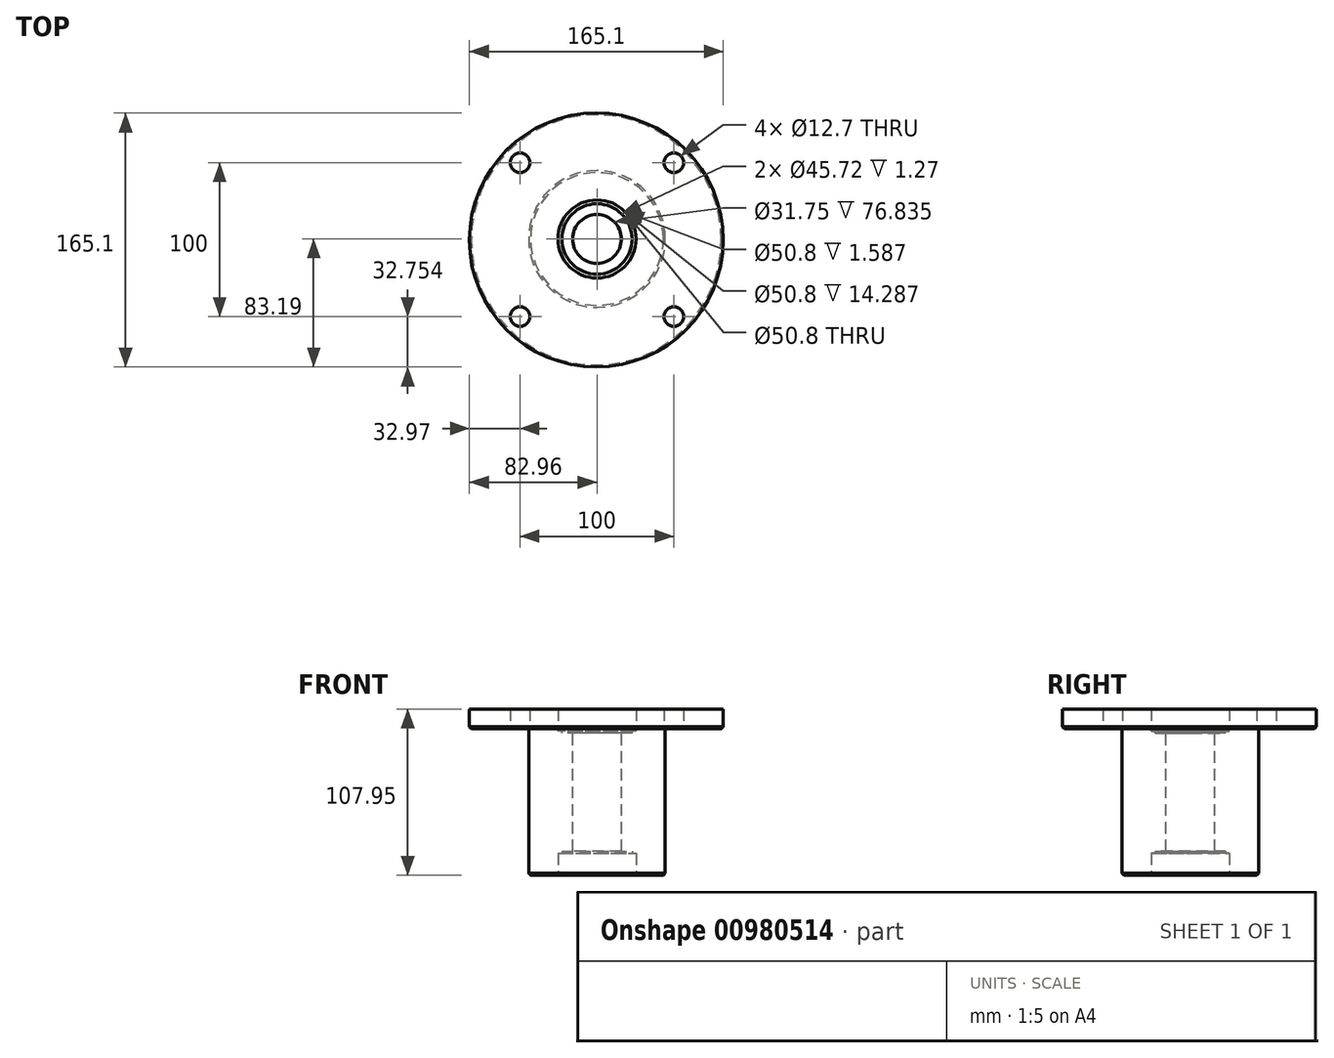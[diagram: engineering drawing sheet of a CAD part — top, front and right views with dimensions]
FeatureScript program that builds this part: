
annotation { "Feature Type Name" : "Feature", "Feature Type Description" : "" }
export const myFeature = defineFeature(function(context is Context, id is Id, definition is map)
    precondition{}
    {
        {
            var Q0;
            Q0=qCreatedBy(makeId("Top.planeOp"),FACE);
            var sketch = newSketch(context, id + "F0", { "sketchPlane" : qUnion([Q0])});
            skCircle(sketch, "E0", {"center": v(-0.4, -0.64) * mm, "radius": 82.55 * mm});
            skSolve(sketch);
        }
        {
            var Q0;
            Q0 = qSketchRegion(id + "F0", true);
            extrude(context, id + "F1", {"entities" : qUnion([Q0]), "depth" : 12.7 * mm, "offsetDistance" : 25.4 * mm});
        }
        {
            var Q0;
            Q0=makeQuery(id+"F1.opExtrude","CAP_FACE",FACE,{"disambiguationData":[OSD([sQuery(id+"F0.wireOp",EDGE,"E0")])],"isStart":true});
            var sketch = newSketch(context, id + "F2", { "sketchPlane" : qUnion([Q0])});
            skCircle(sketch, "E1", {"center": v(0, 0) * mm, "radius": 44.45 * mm});
            skSolve(sketch);
        }
        {
            var Q0;
            Q0=makeQuery(id+"F2.imprint","IMPRINT",FACE,{"disambiguationData":[TD([[makeQuery(id+"F2.imprint","IMPRINT",EDGE,{"derivedFrom":sQuery(id+"F2.wireOp",EDGE,"E1")}),-1.0]])]});
            var sketch = newSketch(context, id + "F3", { "sketchPlane" : qUnion([Q0])});
            skLineSegment(sketch, "E2.bottom", {"start": v(-50, 50.44) * mm, "end": v(50, 50.44) * mm, "construction": true});
            skLineSegment(sketch, "E2.top", {"start": v(-50, -49.56) * mm, "end": v(50, -49.56) * mm, "construction": true});
            skLineSegment(sketch, "E2.left", {"start": v(-50, 50.44) * mm, "end": v(-50, -49.56) * mm, "construction": true});
            skLineSegment(sketch, "E2.right", {"start": v(50, 50.44) * mm, "end": v(50, -49.56) * mm, "construction": true});
            skCircle(sketch, "E3", {"center": v(-50, 50.44) * mm, "radius": 6.35 * mm});
            skCircle(sketch, "E4", {"center": v(50, 50.44) * mm, "radius": 6.35 * mm});
            skCircle(sketch, "E5", {"center": v(50, -49.56) * mm, "radius": 6.35 * mm});
            skCircle(sketch, "E6", {"center": v(-50, -49.56) * mm, "radius": 6.35 * mm});
            skSolve(sketch);
        }
        {
            var Q0;
            Q0=makeQuery(id+"F2.imprint","IMPRINT",FACE,{"disambiguationData":[TD([[makeQuery(id+"F2.imprint","IMPRINT",EDGE,{"derivedFrom":sQuery(id+"F2.wireOp",EDGE,"E1")}),1.0]])]});
            var Q1;
            Q1=sQuery(id+"F2.wireOp",EDGE,"E1");
            extrude(context, id + "F4", {"entities" : qUnion([Q0]), "surfaceEntities" : qUnion([Q1]), "depth" : 95.25 * mm, "offsetDistance" : 25.4 * mm});
        }
        {
            var Q0;
            Q0=makeQuery(id+"F3.imprint","IMPRINT",FACE,{"disambiguationData":[TD([[makeQuery(id+"F3.imprint","IMPRINT",EDGE,{"derivedFrom":sQuery(id+"F3.wireOp",EDGE,"E3")}),1.0]])]});
            var Q1;
            Q1=makeQuery(id+"F3.imprint","IMPRINT",FACE,{"disambiguationData":[TD([[makeQuery(id+"F3.imprint","IMPRINT",EDGE,{"derivedFrom":sQuery(id+"F3.wireOp",EDGE,"E5")}),1.0]])]});
            var Q2;
            Q2=makeQuery(id+"F3.imprint","IMPRINT",FACE,{"disambiguationData":[TD([[makeQuery(id+"F3.imprint","IMPRINT",EDGE,{"derivedFrom":sQuery(id+"F3.wireOp",EDGE,"E4")}),1.0]])]});
            var Q3;
            Q3=makeQuery(id+"F3.imprint","IMPRINT",FACE,{"disambiguationData":[TD([[makeQuery(id+"F3.imprint","IMPRINT",EDGE,{"derivedFrom":sQuery(id+"F3.wireOp",EDGE,"E6")}),1.0]])]});
            var Q4;
            Q4=sQuery(id+"F3.wireOp",EDGE,"E3");
            var Q5;
            Q5=sQuery(id+"F3.wireOp",EDGE,"E4");
            var Q6;
            Q6=sQuery(id+"F3.wireOp",EDGE,"E5");
            var Q7;
            Q7=sQuery(id+"F3.wireOp",EDGE,"E6");
            extrude(context, id + "F5", {"entities" : qUnion([Q0, Q1, Q2, Q3]), "operationType" : NewBodyOperationType.REMOVE, "surfaceEntities" : qUnion([Q4, Q5, Q6, Q7]), "oppositeDirection" : true, "depth" : 25.4 * mm, "offsetDistance" : 25.4 * mm});
        }
        {
            var Q0;
            Q0=makeQuery(id+"F1.opExtrude","CAP_FACE",FACE,{"disambiguationData":[OSD([sQuery(id+"F0.wireOp",EDGE,"E0")])],"isStart":true});
            var sketch = newSketch(context, id + "F6", { "sketchPlane" : qUnion([Q0])});
            skCircle(sketch, "E7", {"center": v(0, 0) * mm, "radius": 15.88 * mm});
            skSolve(sketch);
        }
        {
            var Q0;
            Q0 = qSketchRegion(id + "F6", true);
            extrude(context, id + "F7", {"entities" : qUnion([Q0]), "operationType" : NewBodyOperationType.REMOVE, "depth" : 127 * mm, "offsetDistance" : 25.4 * mm});
        }
        {
            var Q0;
            Q0=makeQuery(id+"F1.opExtrude","CAP_FACE",FACE,{"disambiguationData":[OSD([sQuery(id+"F0.wireOp",EDGE,"E0")])],"isStart":true});
            var sketch = newSketch(context, id + "F8", { "sketchPlane" : qUnion([Q0])});
            skCircle(sketch, "E8", {"center": v(0, 0) * mm, "radius": 25.4 * mm});
            skSolve(sketch);
        }
        {
            var Q0;
            Q0=makeQuery(id+"F8.imprint","IMPRINT",FACE,{"disambiguationData":[TD([[makeQuery(id+"F8.imprint","IMPRINT",EDGE,{"derivedFrom":sQuery(id+"F8.wireOp",EDGE,"E8")}),1.0]])]});
            extrude(context, id + "F9", {"entities" : qUnion([Q0]), "operationType" : NewBodyOperationType.REMOVE, "oppositeDirection" : true, "depth" : 14.29 * mm, "offsetDistance" : 25.4 * mm});
        }
        {
            var Q0;
            Q0=makeQuery(id+"F4.opExtrude","CAP_FACE",FACE,{"disambiguationData":[OSD([sQuery(id+"F2.wireOp",EDGE,"E1")])],"isStart":false});
            var sketch = newSketch(context, id + "F10", { "sketchPlane" : qUnion([Q0])});
            skCircle(sketch, "E9", {"center": v(0, 0) * mm, "radius": 15.88 * mm});
            skSolve(sketch);
        }
        {
            var Q0;
            Q0 = qSketchRegion(id + "F10", true);
            extrude(context, id + "F11", {"entities" : qUnion([Q0]), "operationType" : NewBodyOperationType.REMOVE, "endBound" : BoundingType.THROUGH_ALL, "oppositeDirection" : true, "depth" : 25.4 * mm, "offsetDistance" : 25.4 * mm});
        }
        {
            var Q0;
            Q0=makeQuery(id+"F4.opExtrude","CAP_FACE",FACE,{"disambiguationData":[OSD([sQuery(id+"F2.wireOp",EDGE,"E1")])],"isStart":true});
            var sketch = newSketch(context, id + "F12", { "sketchPlane" : qUnion([Q0])});
            skCircle(sketch, "E10", {"center": v(0, 0) * mm, "radius": 25.4 * mm});
            skSolve(sketch);
        }
        {
            var Q0;
            Q0 = qSketchRegion(id + "F12", true);
            extrude(context, id + "F13", {"entities" : qUnion([Q0]), "operationType" : NewBodyOperationType.REMOVE, "oppositeDirection" : true, "depth" : 1.59 * mm, "offsetDistance" : 25.4 * mm});
        }
        {
            var Q0;
            Q0=makeQuery(id+"F4.opExtrude","CAP_FACE",FACE,{"disambiguationData":[OSD([sQuery(id+"F2.wireOp",EDGE,"E1")])],"isStart":false});
            var sketch = newSketch(context, id + "F14", { "sketchPlane" : qUnion([Q0])});
            skCircle(sketch, "E11", {"center": v(0, 0) * mm, "radius": 25.4 * mm});
            skSolve(sketch);
        }
        {
            var Q0;
            Q0=makeQuery(id+"F14.imprint","IMPRINT",FACE,{"disambiguationData":[TD([[makeQuery(id+"F14.imprint","IMPRINT",EDGE,{"derivedFrom":sQuery(id+"F14.wireOp",EDGE,"E11")}),1.0]])]});
            extrude(context, id + "F15", {"entities" : qUnion([Q0]), "operationType" : NewBodyOperationType.REMOVE, "oppositeDirection" : true, "depth" : 14.29 * mm, "offsetDistance" : 25.4 * mm});
        }
        {
            var Q0;
            Q0=makeQuery(id+"F15.boolean.opBoolean","COPY",FACE,{"derivedFrom":makeQuery(id+"F15.opExtrude","CAP_FACE",FACE,{"disambiguationData":[OSD([sQuery(id+"F10.wireOp",EDGE,"E9"),sQuery(id+"F14.wireOp",EDGE,"E11")])],"isStart":false})});
            var sketch = newSketch(context, id + "F16", { "sketchPlane" : qUnion([Q0])});
            skCircle(sketch, "E12", {"center": v(0, 0) * mm, "radius": 22.86 * mm});
            skSolve(sketch);
        }
        {
            var Q0;
            Q0 = qSketchRegion(id + "F16", true);
            extrude(context, id + "F17", {"entities" : qUnion([Q0]), "operationType" : NewBodyOperationType.REMOVE, "oppositeDirection" : true, "depth" : 1.27 * mm, "offsetDistance" : 25.4 * mm});
        }
        {
            var Q0;
            Q0=makeQuery(id+"F13.boolean.opBoolean","COPY",FACE,{"derivedFrom":makeQuery(id+"F13.opExtrude","CAP_FACE",FACE,{"disambiguationData":[OSD([sQuery(id+"F12.wireOp",EDGE,"E10")])],"isStart":false})});
            var sketch = newSketch(context, id + "F18", { "sketchPlane" : qUnion([Q0])});
            skCircle(sketch, "E13", {"center": v(0, 0) * mm, "radius": 22.86 * mm});
            skSolve(sketch);
        }
        {
            var Q0;
            Q0 = qSketchRegion(id + "F18", true);
            extrude(context, id + "F19", {"entities" : qUnion([Q0]), "operationType" : NewBodyOperationType.REMOVE, "oppositeDirection" : true, "depth" : 1.27 * mm, "offsetDistance" : 25.4 * mm});
        }
        {
            var Q0;
            Q0=makeQuery(id+"F1.opExtrude","CAP_EDGE",EDGE,{"disambiguationData":[OSD([sQuery(id+"F0.wireOp",EDGE,"E0")])],"isStart":true});
            chamfer(context, id + "F20", {"entities" : qUnion([Q0]), "width" : 1.27 * mm, "tangentPropagation" : true});
        }
        {
            var Q0;
            Q0=makeQuery(id+"F4.opExtrude","CAP_EDGE",EDGE,{"disambiguationData":[OSD([sQuery(id+"F2.wireOp",EDGE,"E1")])],"isStart":false});
            chamfer(context, id + "F21", {"entities" : qUnion([Q0]), "width" : 1.27 * mm, "tangentPropagation" : true});
        }
    });
